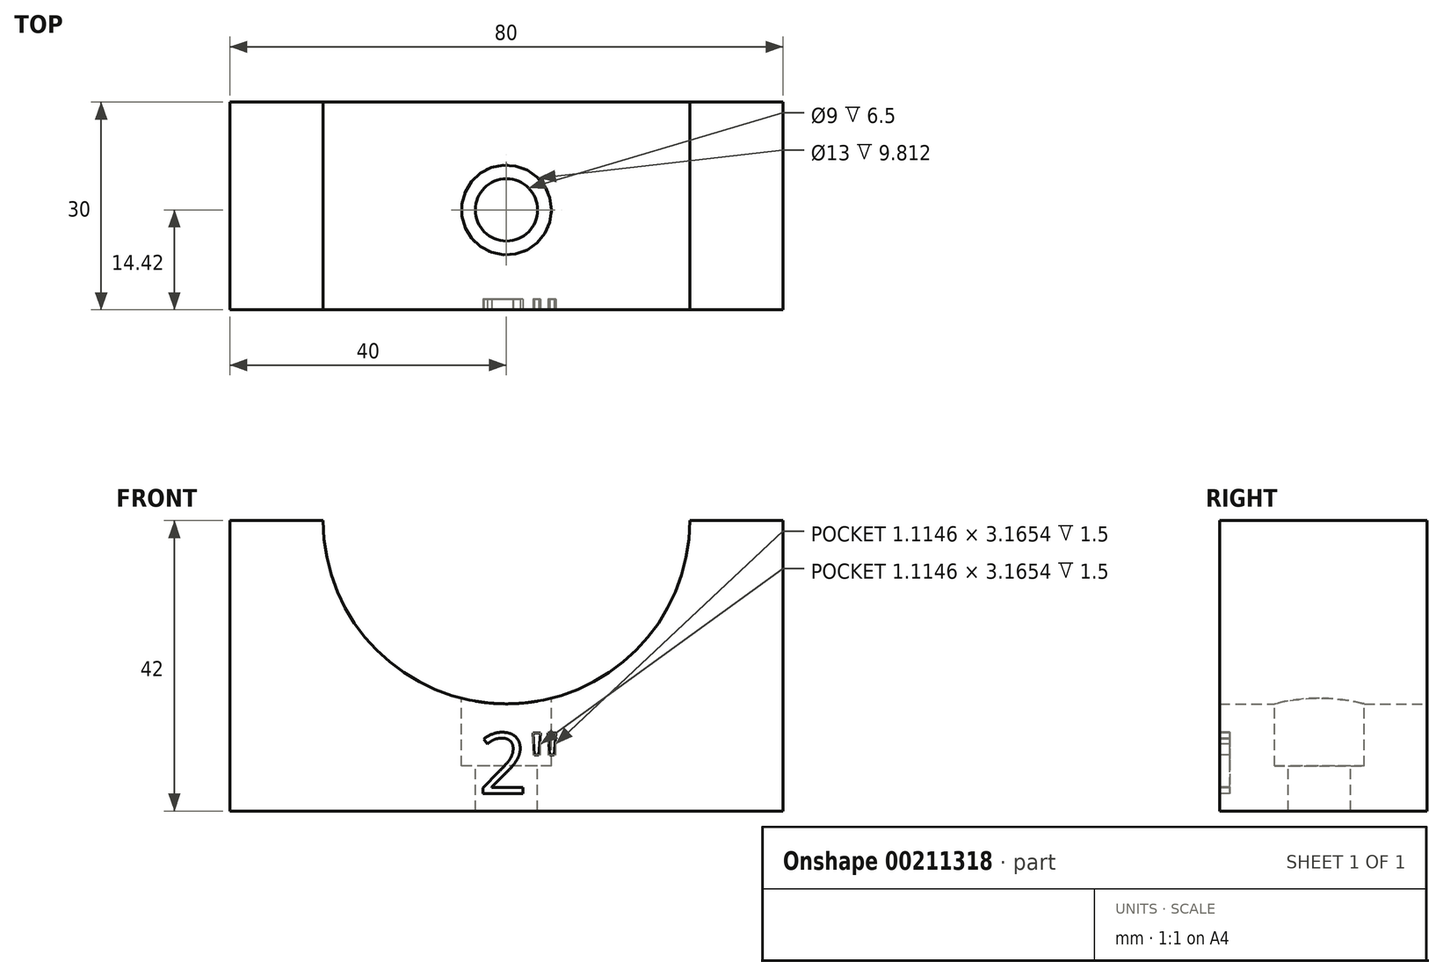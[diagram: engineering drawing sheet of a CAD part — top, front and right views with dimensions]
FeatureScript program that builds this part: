
annotation { "Feature Type Name" : "Feature", "Feature Type Description" : "" }
export const myFeature = defineFeature(function(context is Context, id is Id, definition is map)
    precondition{}
    {
        {
            var Q0;
            Q0=qCreatedBy(makeId("Front.planeOp"),FACE);
            var sketch = newSketch(context, id + "F0", { "sketchPlane" : qUnion([Q0])});
            skLineSegment(sketch, "E0.bottom", {"start": v(40, -30) * mm, "end": v(-40, -30) * mm});
            skLineSegment(sketch, "E0.top", {"start": v(40, 30) * mm, "end": v(-40, 30) * mm});
            skLineSegment(sketch, "E0.left", {"start": v(40, -30) * mm, "end": v(40, 30) * mm});
            skLineSegment(sketch, "E0.right", {"start": v(-40, -30) * mm, "end": v(-40, 30) * mm});
            skPoint(sketch, "E0.middle", {"position": v(0, 0) * mm});
            skPoint(sketch, "E1", {"position": v(-40, 30) * mm});
            skPoint(sketch, "E2", {"position": v(40, 30) * mm});
            skLineSegment(sketch, "E3", {"start": v(0, 0) * mm, "end": v(0, 12) * mm});
            skPoint(sketch, "E4", {"position": v(0, 30) * mm});
            skPoint(sketch, "E5", {"position": v(0, 12) * mm});
            skCircle(sketch, "E6", {"center": v(0, 12) * mm, "radius": 26.5 * mm});
            skLineSegment(sketch, "E7", {"start": v(40, 12) * mm, "end": v(-40, 12) * mm});
            skSolve(sketch);
        }
        {
            var Q0;
            Q0=makeQuery(id+"F0.imprint","IMPRINT",FACE,{"disambiguationData":[TD([[makeQuery(id+"F0.imprint","IMPRINT",EDGE,{"derivedFrom":sQuery(id+"F0.wireOp",EDGE,"E0.bottom")}),-1.0]])]});
            extrude(context, id + "F1", {"entities" : qUnion([Q0]), "depth" : 30 * mm});
        }
        {
            var Q0;
            Q0=qCreatedBy(makeId("Top.planeOp"),FACE);
            var sketch = newSketch(context, id + "F2", { "sketchPlane" : qUnion([Q0])});
            skLineSegment(sketch, "E8", {"start": v(0, -0.58) * mm, "end": v(0, -30.58) * mm});
            skPoint(sketch, "E9", {"position": v(0, -15.58) * mm});
            skSolve(sketch);
        }
        {
            var Q0;
            Q0=sQuery(id+"F2.wireOp",VERTEX,"E9");
            var Q1;
            Q1=makeQuery(id+"F1.opExtrude","SWEPT_BODY",BODY,{"disambiguationData":[OSD([sQuery(id+"F0.wireOp",EDGE,"E0.bottom"),sQuery(id+"F0.wireOp",EDGE,"E0.left"),sQuery(id+"F0.wireOp",EDGE,"E0.right"),sQuery(id+"F0.wireOp",EDGE,"E6"),sQuery(id+"F0.wireOp",EDGE,"E7")])]});
            hole(context, id + "F3", {"style" : HoleStyle.C_BORE, "endStyle" : HoleEndStyle.THROUGH, "holeDiameter" : 9 * mm, "cBoreDiameter" : 13 * mm, "cBoreDepth" : 9 * mm, "locations" : qUnion([Q0]), "scope" : qUnion([Q1]), "isTappedThrough" : true});
        }
        {
            var Q0;
            Q0=makeQuery(id+"F1.opExtrude","CAP_FACE",FACE,{"disambiguationData":[OSD([sQuery(id+"F0.wireOp",EDGE,"E0.bottom"),sQuery(id+"F0.wireOp",EDGE,"E0.left"),sQuery(id+"F0.wireOp",EDGE,"E0.right"),sQuery(id+"F0.wireOp",EDGE,"E6"),sQuery(id+"F0.wireOp",EDGE,"E7")])],"isStart":false});
            var sketch = newSketch(context, id + "F4", { "sketchPlane" : qUnion([Q0])});
            skText(sketch, "E10", { "text": "2\"", "fontName": "OpenSans-Regular.ttf"});
            skLineSegment(sketch, "E11", {"start": v(-40, -30) * mm, "end": v(40, -30) * mm});
            const initialGuessF4  = {"E10": [-0.004, -0.0275, 1, 0, 0.00884]};
            skSetInitialGuess(sketch, initialGuessF4);
            skSolve(sketch);
        }
        {
            var Q0;
            Q0 = qSketchRegion(id + "F4", true);
            extrude(context, id + "F5", {"entities" : qUnion([Q0]), "operationType" : NewBodyOperationType.REMOVE, "oppositeDirection" : true, "depth" : 1.5 * mm});
        }
    });
